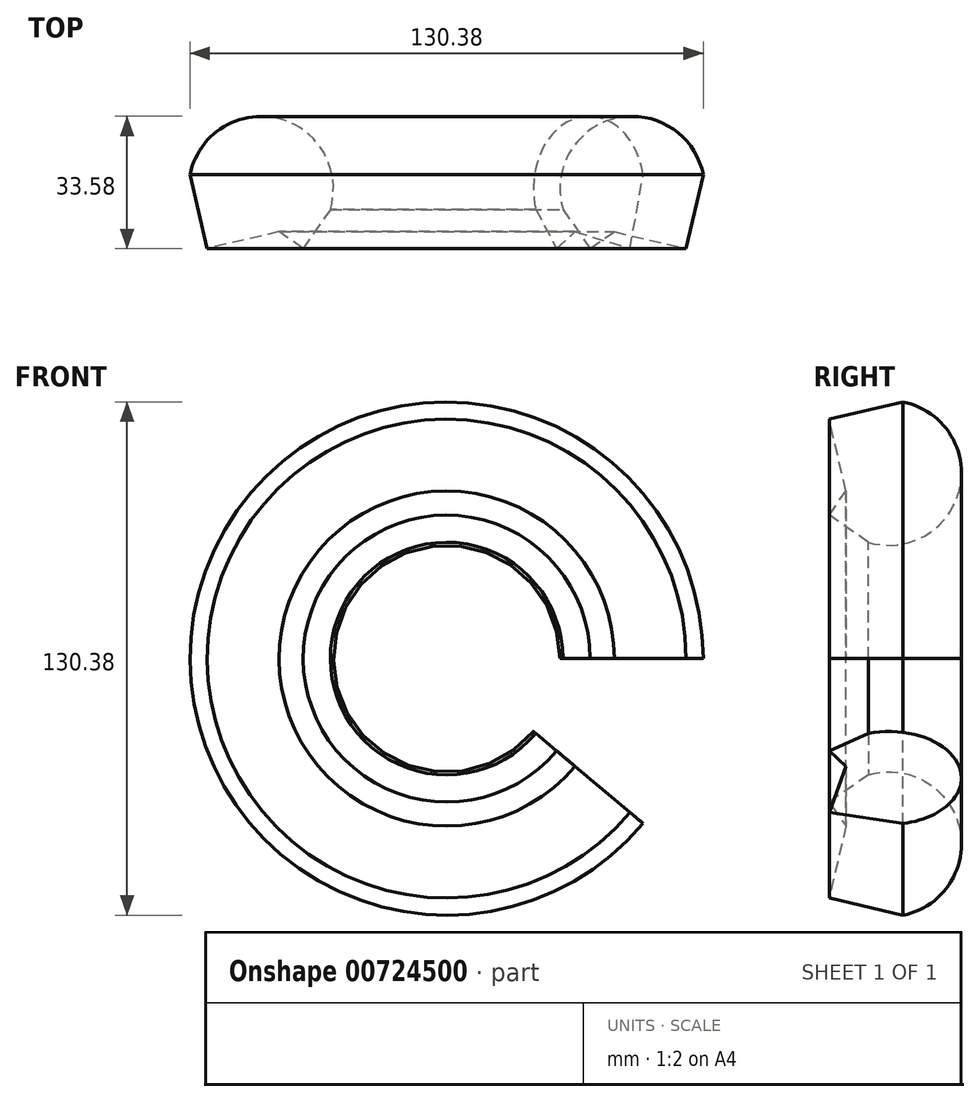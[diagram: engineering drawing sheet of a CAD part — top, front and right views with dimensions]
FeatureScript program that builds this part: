
annotation { "Feature Type Name" : "Feature", "Feature Type Description" : "" }
export const myFeature = defineFeature(function(context is Context, id is Id, definition is map)
    precondition{}
    {
        {
            var Q0;
            Q0=qCreatedBy(makeId("Top.planeOp"),FACE);
            var sketch = newSketch(context, id + "F0", { "sketchPlane" : qUnion([Q0])});
            skLineSegment(sketch, "E0", {"start": v(29.55, 15.53) * mm, "end": v(36.45, 5.58) * mm});
            skLineSegment(sketch, "E1", {"start": v(36.45, 5.58) * mm, "end": v(42.57, 9.83) * mm});
            skLineSegment(sketch, "E2", {"start": v(42.57, 9.83) * mm, "end": v(60.82, 5.58) * mm});
            skLineSegment(sketch, "E3", {"start": v(60.82, 5.58) * mm, "end": v(65.19, 24.35) * mm});
            skArc(sketch, "E4", {"start": v(65.19, 24.35) * mm, "mid": v(42.75, 38.62) * mm, "end": v(29.55, 15.53) * mm});
            skSolve(sketch);
        }
        {
            var Q0;
            Q0=qCreatedBy(makeId("Top.planeOp"),FACE);
            var sketch = newSketch(context, id + "F1", { "sketchPlane" : qUnion([Q0])});
            skLineSegment(sketch, "E5", {"start": v(0, 40.09) * mm, "end": v(0, 0) * mm});
            skSolve(sketch);
        }
        {
            var Q0;
            Q0=makeQuery(id+"F0.imprint","IMPRINT",FACE,{"disambiguationData":[TD([[makeQuery(id+"F0.imprint","IMPRINT",EDGE,{"derivedFrom":sQuery(id+"F0.wireOp",EDGE,"E0")}),1.0]])]});
            var Q1;
            Q1=sQuery(id+"F1.wireOp",EDGE,"E5");
            revolve(context, id + "F2", {"surfaceOperationType" : NewSurfaceOperationType.NEW, "entities" : qUnion([Q0]), "axis" : qUnion([Q1]), "revolveType" : RevolveType.ONE_DIRECTION, "angle" : 320 * degree});
        }
    });
